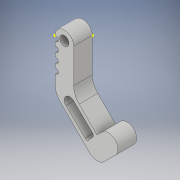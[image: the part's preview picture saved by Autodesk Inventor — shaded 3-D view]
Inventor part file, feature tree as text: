
AUTODESK INVENTOR PART (.ipt)
format: ipt  version: 2018.1 (Build 221171000, 171)  size: 250,880 bytes
history: native  units: in
note: dims shown in document units (in); Inventor stores cm internally (conversion verified against a paired STEP export)
features: sketch x14, extrude x6, chamfer x4, other x3, fillet x1
ambient origin geometry x8: Origin, YZ Plane, XZ Plane, XY Plane, X Axis, Y Axis, Z Axis, Center Point
bodies: Solid1 (feature_tree)
feature tree (28):
  other  "Claw_design_gear_1.ipt"
  sketch  "Sketch6"  dims[d7=0.15in d8=0.0in d9=0.05in d10=0.125in d11=45.0deg]
  sketch  "Sketch7"  dims[d12=0.15in d13=0.0in d14=0.05in d15=0.125in d16=45.0deg d17=0.05in d18=0.125in d19=45.0deg]
  extrude  "Extrusion1"  Depth=0.886in TaperAngle=0.0deg
  sketch  "Sketch8"  dims[d20=0.05in d21=0.125in d22=45.0deg d23=0.75in d24=0.886in d25=0.0in]
  extrude  "Extrusion2"  Depth=0.15in TaperAngle=0.0deg
  sketch  "Sketch12"
  sketch  "Sketch13"
  extrude  "Extrusion3"  Depth=0.125in TaperAngle=45.0deg
  extrude  "Extrusion4"  Depth=0.125in TaperAngle=45.0deg
  sketch  "Sketch15"
  chamfer  "Chamfer1"  Distance=0.125in Angle=45.0deg
  extrude  "Extrusion5"  Depth=0.886in
  chamfer  "Chamfer2"  Distance=0.886in
  chamfer  "Chamfer3"  [1 undecoded]
  chamfer  "Chamfer4"  [1 undecoded]
  sketch  "Sketch16"
  sketch  "Sketch17"
  extrude  "Extrusion6"  [1 undecoded]
  fillet  "Fillet1"  [1 undecoded]
  other  "Solid1::Claw_design_gear_1.ipt"
  other  "TaggingFeature1"
  sketch  "Sketch2"  dims[d0=0.5906in d1=0.886in d2=0.0in]
  sketch  "Sketch3"  dims[d3=0.15in d4=0.0in d5=0.15in d6=0.0in]
  sketch  "Sketch9"  dims[d26=0.125in]
  sketch  "Sketch11"
  sketch  "Sketch10"
  sketch  "Sketch14"
note: 4 required parameter values undecoded (feature->parameter linkage not recoverable at this tier; creation-order binding heuristic only, values carry confidence <= 0.55)
